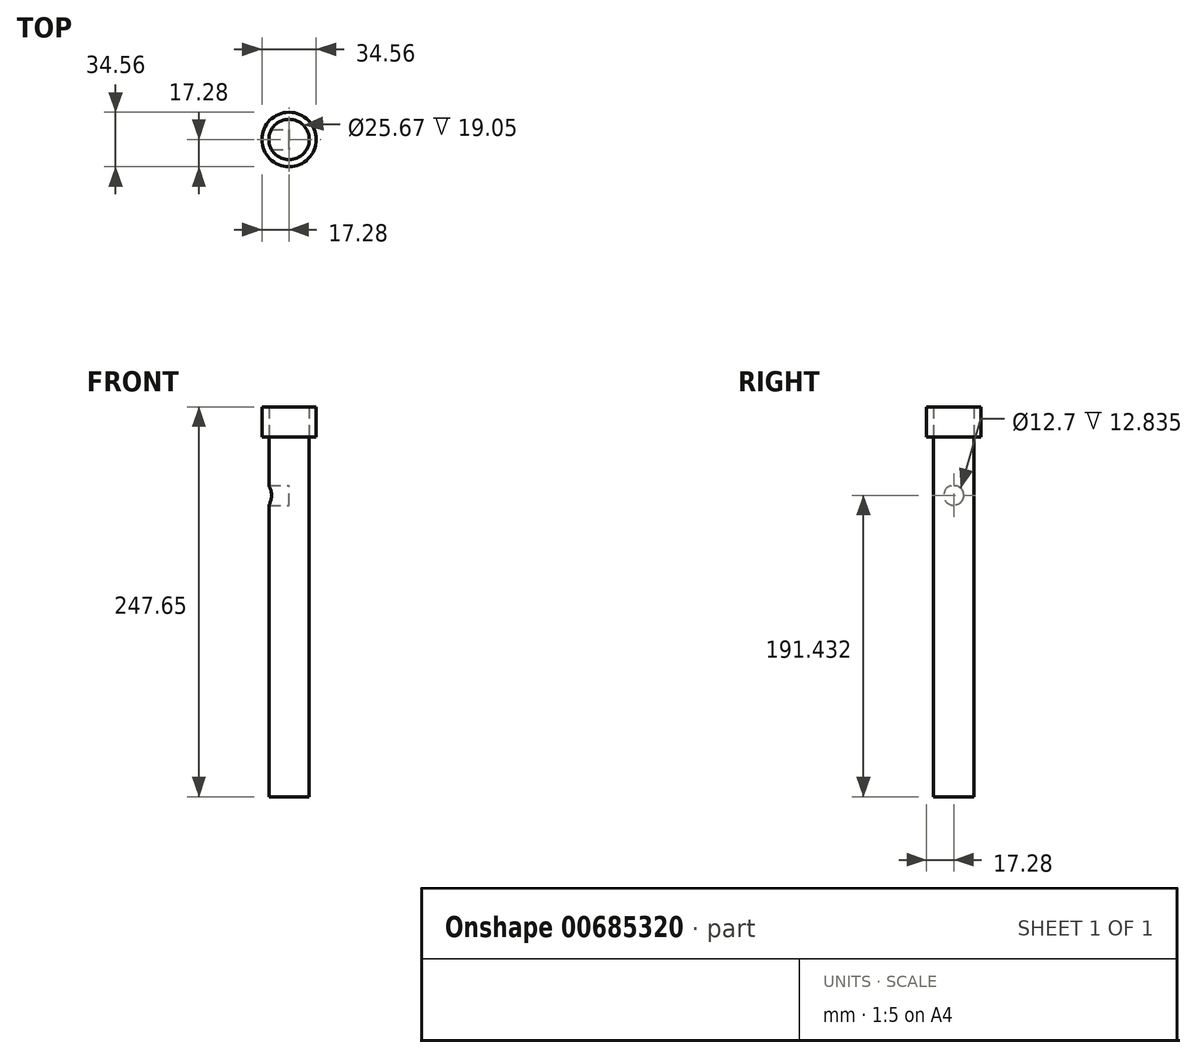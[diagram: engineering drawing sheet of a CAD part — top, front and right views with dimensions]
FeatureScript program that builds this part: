
annotation { "Feature Type Name" : "Feature", "Feature Type Description" : "" }
export const myFeature = defineFeature(function(context is Context, id is Id, definition is map)
    precondition{}
    {
        {
            var Q0;
            Q0=qCreatedBy(makeId("Top.planeOp"),FACE);
            var sketch = newSketch(context, id + "F0", { "sketchPlane" : qUnion([Q0])});
            skCircle(sketch, "E0", {"center": v(0, 0) * mm, "radius": 12.84 * mm});
            skSolve(sketch);
        }
        {
            var Q0;
            Q0=makeQuery(id+"F0.imprint","IMPRINT",FACE,{"disambiguationData":[TD([[makeQuery(id+"F0.imprint","IMPRINT",EDGE,{"derivedFrom":sQuery(id+"F0.wireOp",EDGE,"E0")}),1.0]])]});
            extrude(context, id + "F1", {"entities" : qUnion([Q0]), "endBound" : BoundingType.SYMMETRIC, "depth" : 228.6 * mm, "offsetDistance" : 25.4 * mm});
        }
        {
            var Q0;
            Q0=qCreatedBy(makeId("Right.planeOp"),FACE);
            var sketch = newSketch(context, id + "F2", { "sketchPlane" : qUnion([Q0])});
            skPoint(sketch, "E1", {"position": v(0, 77.13) * mm});
            skSolve(sketch);
        }
        {
            var Q0;
            Q0=makeQuery(id+"F1.opExtrude","CAP_FACE",FACE,{"disambiguationData":[OSD([sQuery(id+"F0.wireOp",EDGE,"E0")])],"isStart":false});
            var sketch = newSketch(context, id + "F3", { "sketchPlane" : qUnion([Q0])});
            skCircle(sketch, "E2", {"center": v(0, 0) * mm, "radius": 17.28 * mm});
            skSolve(sketch);
        }
        {
            var Q0;
            Q0=makeQuery(id+"F3.imprint","IMPRINT",FACE,{"disambiguationData":[TD([[makeQuery(id+"F3.imprint","IMPRINT",EDGE,{"derivedFrom":sQuery(id+"F3.wireOp",EDGE,"E2")}),1.0]])]});
            extrude(context, id + "F4", {"entities" : qUnion([Q0]), "depth" : 19.05 * mm, "offsetDistance" : 25.4 * mm});
        }
        {
            var Q0;
            Q0=sQuery(id+"F2.wireOp",VERTEX,"E1");
            var Q1;
            Q1=makeQuery(id+"F1.opExtrude","SWEPT_BODY",BODY,{"disambiguationData":[OSD([sQuery(id+"F0.wireOp",EDGE,"E0")])]});
            hole(context, id + "F5", {"style" : HoleStyle.SIMPLE, "endStyle" : HoleEndStyle.BLIND, "holeDiameter" : 12.7 * mm, "majorDiameter" : 6.35 * mm, "holeDepth" : 50.8 * mm, "isTappedThrough" : true, "tappedDepth" : 12.7 * mm, "tapClearance" : 3, "locations" : qUnion([Q0]), "scope" : qUnion([Q1])});
        }
    });
